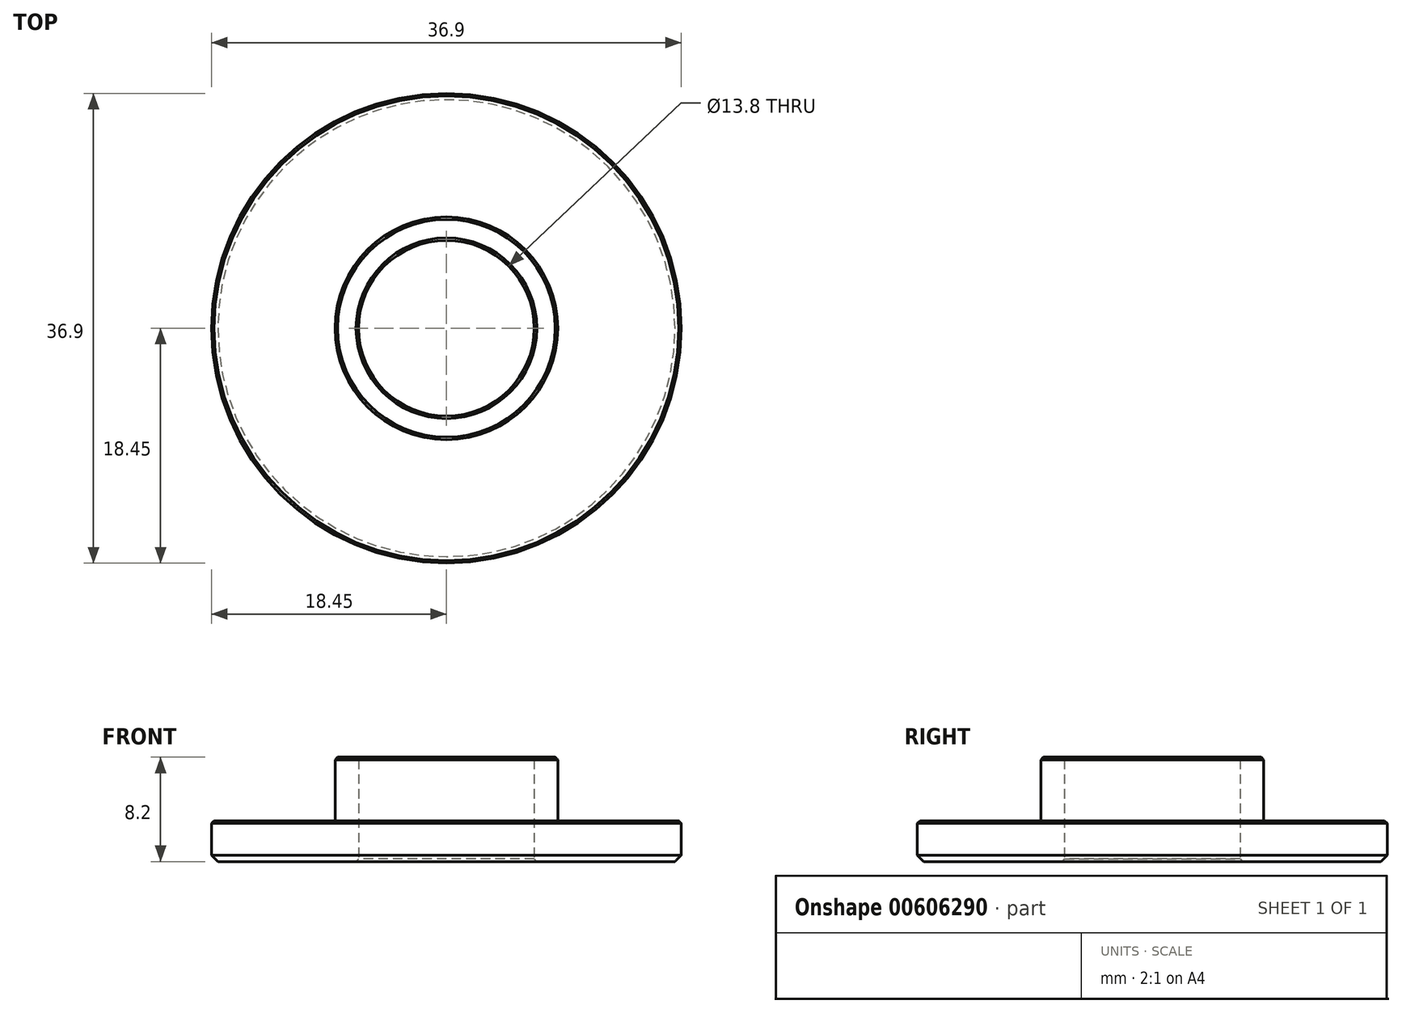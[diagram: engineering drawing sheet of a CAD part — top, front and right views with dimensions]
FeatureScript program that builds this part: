
annotation { "Feature Type Name" : "Feature", "Feature Type Description" : "" }
export const myFeature = defineFeature(function(context is Context, id is Id, definition is map)
    precondition{}
    {
        {
            var Q0;
            Q0=qCreatedBy(makeId("Top.planeOp"),FACE);
            var sketch = newSketch(context, id + "F0", { "sketchPlane" : qUnion([Q0])});
            skCircle(sketch, "E0", {"center": v(0, 0) * mm, "radius": 6.9 * mm});
            skCircle(sketch, "E1", {"center": v(0, 0) * mm, "radius": 18.45 * mm});
            skSolve(sketch);
        }
        {
            var Q0;
            Q0 = qSketchRegion(id + "F0", true);
            extrude(context, id + "F1", {"entities" : qUnion([Q0]), "depth" : 3.2 * mm, "offsetDistance" : 25 * mm});
        }
        {
            var Q0;
            Q0=makeQuery(id+"F1.opExtrude","CAP_FACE",FACE,{"disambiguationData":[OSD([sQuery(id+"F0.wireOp",EDGE,"E0"),sQuery(id+"F0.wireOp",EDGE,"E1")])],"isStart":false});
            var sketch = newSketch(context, id + "F2", { "sketchPlane" : qUnion([Q0])});
            skCircle(sketch, "E2.0", {"center": v(0, 0) * mm, "radius": 6.9 * mm});
            skCircle(sketch, "E3", {"center": v(0, 0) * mm, "radius": 8.75 * mm});
            skSolve(sketch);
        }
        {
            var Q0;
            Q0 = qSketchRegion(id + "F2", true);
            extrude(context, id + "F3", {"entities" : qUnion([Q0]), "operationType" : NewBodyOperationType.ADD, "depth" : 5 * mm, "offsetDistance" : 25 * mm});
        }
        {
            var Q0;
            Q0=makeQuery(id+"F1.opExtrude","CAP_EDGE",EDGE,{"disambiguationData":[OSD([sQuery(id+"F0.wireOp",EDGE,"E1")])],"isStart":true});
            chamfer(context, id + "F4", {"entities" : qUnion([Q0]), "width" : 0.5 * mm, "tangentPropagation" : true});
        }
        {
            var Q0;
            Q0=makeQuery(id+"F1.opExtrude","CAP_EDGE",EDGE,{"disambiguationData":[OSD([sQuery(id+"F0.wireOp",EDGE,"E0")])],"isStart":true});
            var Q1;
            Q1=makeQuery(id+"F3.opExtrude","CAP_EDGE",EDGE,{"disambiguationData":[OSD([sQuery(id+"F2.wireOp",EDGE,"E2.0")])],"isStart":false});
            var Q2;
            Q2=makeQuery(id+"F3.opExtrude","CAP_EDGE",EDGE,{"disambiguationData":[OSD([sQuery(id+"F2.wireOp",EDGE,"E3")])],"isStart":false});
            var Q3;
            Q3=makeQuery(id+"F3.opExtrude","CAP_EDGE",EDGE,{"disambiguationData":[OSD([sQuery(id+"F2.wireOp",EDGE,"E3")])],"isStart":true});
            var Q4;
            Q4=makeQuery(id+"F1.opExtrude","CAP_EDGE",EDGE,{"disambiguationData":[OSD([sQuery(id+"F0.wireOp",EDGE,"E1")])],"isStart":false});
            chamfer(context, id + "F5", {"entities" : qUnion([Q0, Q1, Q2, Q3, Q4]), "width" : 0.2 * mm, "tangentPropagation" : true});
        }
    });
